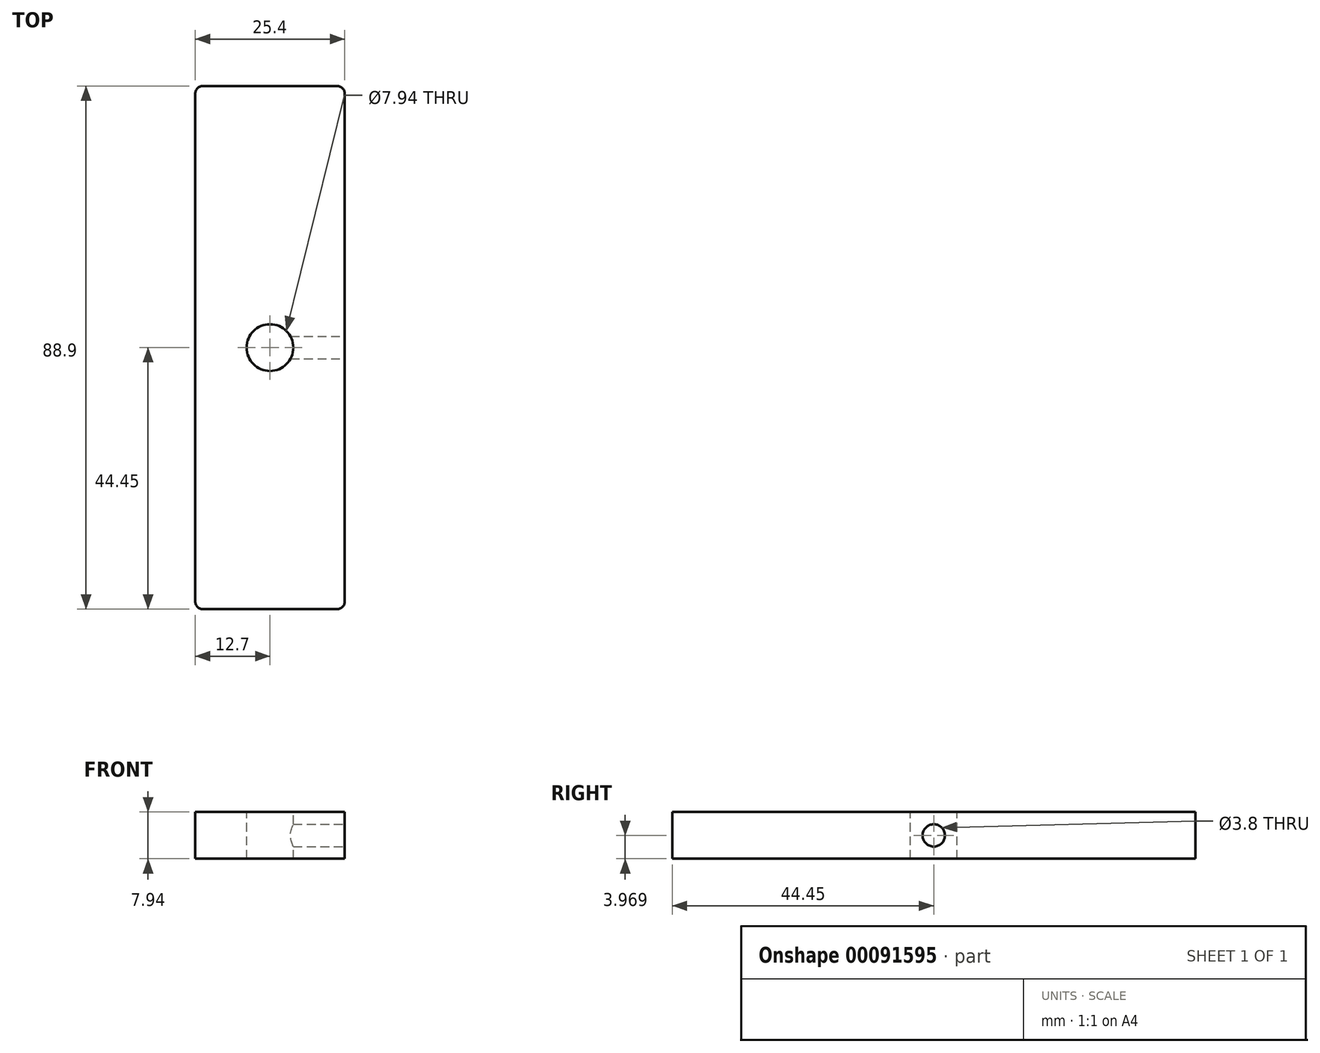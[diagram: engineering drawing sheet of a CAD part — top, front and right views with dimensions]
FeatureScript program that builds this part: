
annotation { "Feature Type Name" : "Feature", "Feature Type Description" : "" }
export const myFeature = defineFeature(function(context is Context, id is Id, definition is map)
    precondition{}
    {
        {
            var Q0;
            Q0=qCreatedBy(makeId("Top.planeOp"),FACE);
            var sketch = newSketch(context, id + "F0", { "sketchPlane" : qUnion([Q0])});
            skLineSegment(sketch, "E0.bottom", {"start": v(0, 0) * mm, "end": v(25.4, 0) * mm});
            skLineSegment(sketch, "E0.top", {"start": v(0, 88.9) * mm, "end": v(25.4, 88.9) * mm});
            skLineSegment(sketch, "E0.left", {"start": v(0, 0) * mm, "end": v(0, 88.9) * mm});
            skLineSegment(sketch, "E0.right", {"start": v(25.4, 0) * mm, "end": v(25.4, 88.9) * mm});
            skSolve(sketch);
        }
        {
            var Q0;
            Q0=makeQuery(id+"F0.imprint","IMPRINT",FACE,{"disambiguationData":[TD([[makeQuery(id+"F0.imprint","IMPRINT",EDGE,{"derivedFrom":sQuery(id+"F0.wireOp",EDGE,"E0.bottom")}),1.0]])]});
            extrude(context, id + "F1", {"entities" : qUnion([Q0]), "depth" : 7.94 * mm});
        }
        {
            var Q0;
            Q0=makeQuery(id+"F1.opExtrude","CAP_FACE",FACE,{"disambiguationData":[OSD([sQuery(id+"F0.wireOp",EDGE,"E0.bottom"),sQuery(id+"F0.wireOp",EDGE,"E0.top"),sQuery(id+"F0.wireOp",EDGE,"E0.left"),sQuery(id+"F0.wireOp",EDGE,"E0.right")])],"isStart":false});
            var sketch = newSketch(context, id + "F2", { "sketchPlane" : qUnion([Q0])});
            skCircle(sketch, "E1", {"center": v(12.7, 44.45) * mm, "radius": 3.97 * mm});
            skSolve(sketch);
        }
        {
            var Q0;
            Q0=makeQuery(id+"F2.imprint","IMPRINT",FACE,{"disambiguationData":[TD([[makeQuery(id+"F2.imprint","IMPRINT",EDGE,{"derivedFrom":sQuery(id+"F2.wireOp",EDGE,"E1")}),1.0]])]});
            extrude(context, id + "F3", {"entities" : qUnion([Q0]), "operationType" : NewBodyOperationType.REMOVE, "endBound" : BoundingType.UP_TO_NEXT, "oppositeDirection" : true, "depth" : 25.4 * mm});
        }
        {
            var Q0;
            Q0=makeQuery(id+"F1.opExtrude","SWEPT_FACE",FACE,{"disambiguationData":[OSD([sQuery(id+"F0.wireOp",EDGE,"E0.right")])]});
            var sketch = newSketch(context, id + "F4", { "sketchPlane" : qUnion([Q0])});
            skPoint(sketch, "E2", {"position": v(44.45, 3.97) * mm});
            skSolve(sketch);
        }
        {
            var Q0;
            Q0=sQuery(id+"F4.wireOp",VERTEX,"E2");
            var Q1;
            Q1=makeQuery(id+"F1.opExtrude","SWEPT_BODY",BODY,{"disambiguationData":[OSD([sQuery(id+"F0.wireOp",EDGE,"E0.bottom"),sQuery(id+"F0.wireOp",EDGE,"E0.top"),sQuery(id+"F0.wireOp",EDGE,"E0.left"),sQuery(id+"F0.wireOp",EDGE,"E0.right")])]});
            hole(context, id + "F5", {"style" : HoleStyle.SIMPLE, "endStyle" : HoleEndStyle.BLIND, "standardTappedOrClearance" : lookupTablePath({ "standard" : "ANSI", "engagement" : "75%", "pitch" : "24 tpi", "size" : "#10", "type" : "Tapped" }), "standardBlindInLast" : lookupTablePath({ "standard" : "ANSI", "engagement" : "75%", "pitch" : "24 tpi", "size" : "#10", "type" : "Tapped" }), "holeDiameter" : 3.8 * mm, "holeDepth" : 12.7 * mm, "locations" : qUnion([Q0]), "scope" : qUnion([Q1]), "majorDiameter" : 4.83 * mm});
        }
        {
            var Q0;
            Q0=makeQuery(id+"F1.opExtrude","SWEPT_EDGE",EDGE,{"disambiguationData":[OSD([sQuery(id+"F0.wireOp",EDGE,"E0.top"),sQuery(id+"F0.wireOp",EDGE,"E0.right")])]});
            var Q1;
            Q1=makeQuery(id+"F1.opExtrude","SWEPT_EDGE",EDGE,{"disambiguationData":[OSD([sQuery(id+"F0.wireOp",EDGE,"E0.top"),sQuery(id+"F0.wireOp",EDGE,"E0.left")])]});
            var Q2;
            Q2=makeQuery(id+"F1.opExtrude","SWEPT_EDGE",EDGE,{"disambiguationData":[OSD([sQuery(id+"F0.wireOp",EDGE,"E0.bottom"),sQuery(id+"F0.wireOp",EDGE,"E0.right")])]});
            var Q3;
            Q3=makeQuery(id+"F1.opExtrude","SWEPT_EDGE",EDGE,{"disambiguationData":[OSD([sQuery(id+"F0.wireOp",EDGE,"E0.bottom"),sQuery(id+"F0.wireOp",EDGE,"E0.left")])]});
            fillet(context, id + "F6", {"entities" : qUnion([Q0, Q1, Q2, Q3]), "radius" : 1.27 * mm, "tangentPropagation" : true, "allowEdgeOverflow" : false});
        }
    });
